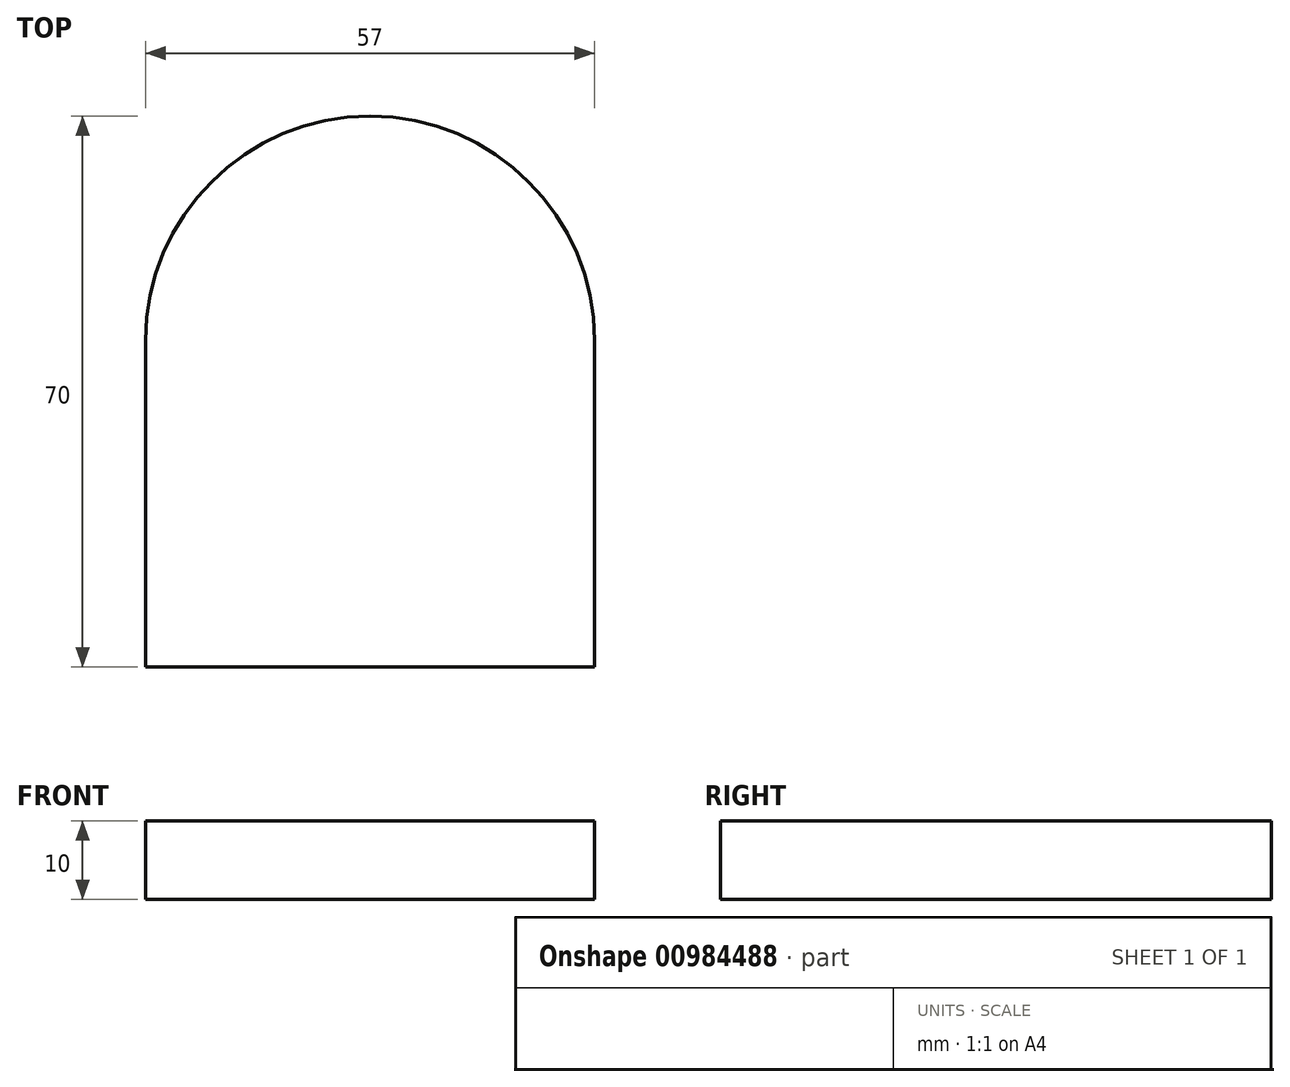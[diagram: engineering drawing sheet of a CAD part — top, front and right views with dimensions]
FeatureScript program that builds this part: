
annotation { "Feature Type Name" : "Feature", "Feature Type Description" : "" }
export const myFeature = defineFeature(function(context is Context, id is Id, definition is map)
    precondition{}
    {
        {
            var Q0;
            Q0=qCreatedBy(makeId("Top.planeOp"),FACE);
            var sketch = newSketch(context, id + "F0", { "sketchPlane" : qUnion([Q0])});
            skLineSegment(sketch, "E0.top", {"start": v(28.5, -20.75) * mm, "end": v(-28.5, -20.75) * mm});
            skLineSegment(sketch, "E0.left", {"start": v(28.5, 20.75) * mm, "end": v(28.5, -20.75) * mm});
            skLineSegment(sketch, "E0.right", {"start": v(-28.5, 20.75) * mm, "end": v(-28.5, -20.75) * mm});
            skPoint(sketch, "E0.middle", {"position": v(0, 0) * mm});
            skArc(sketch, "E1", {"start": v(-28.5, 20.75) * mm, "mid": v(0, 49.25) * mm, "end": v(28.5, 20.75) * mm});
            skSolve(sketch);
        }
        {
            var Q0;
            Q0 = qSketchRegion(id + "F0", true);
            extrude(context, id + "F1", {"entities" : qUnion([Q0]), "depth" : 10 * mm, "offsetDistance" : 25 * mm});
        }
    });
